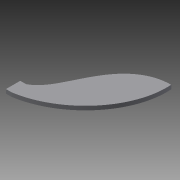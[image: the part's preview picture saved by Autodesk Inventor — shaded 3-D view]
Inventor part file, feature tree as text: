
AUTODESK INVENTOR PART (.ipt)
format: ipt  version: 2015 (Build 190159000, 159)  size: 77,312 bytes
history: native  units: mm
features: extrude x1, sketch x1
ambient origin geometry x8: Origin, YZ Plane, XZ Plane, XY Plane, X Axis, Y Axis, Z Axis, Center Point
bodies: Solid1 (feature_tree)
feature tree (2):
  extrude  "Extrusion1"  [1 undecoded]
  sketch  "Sketch1"  dims[d4=5.5mm d5=0.0mm]
note: 1 required parameter value undecoded (feature->parameter linkage not recoverable at this tier; creation-order binding heuristic only, values carry confidence <= 0.55)
